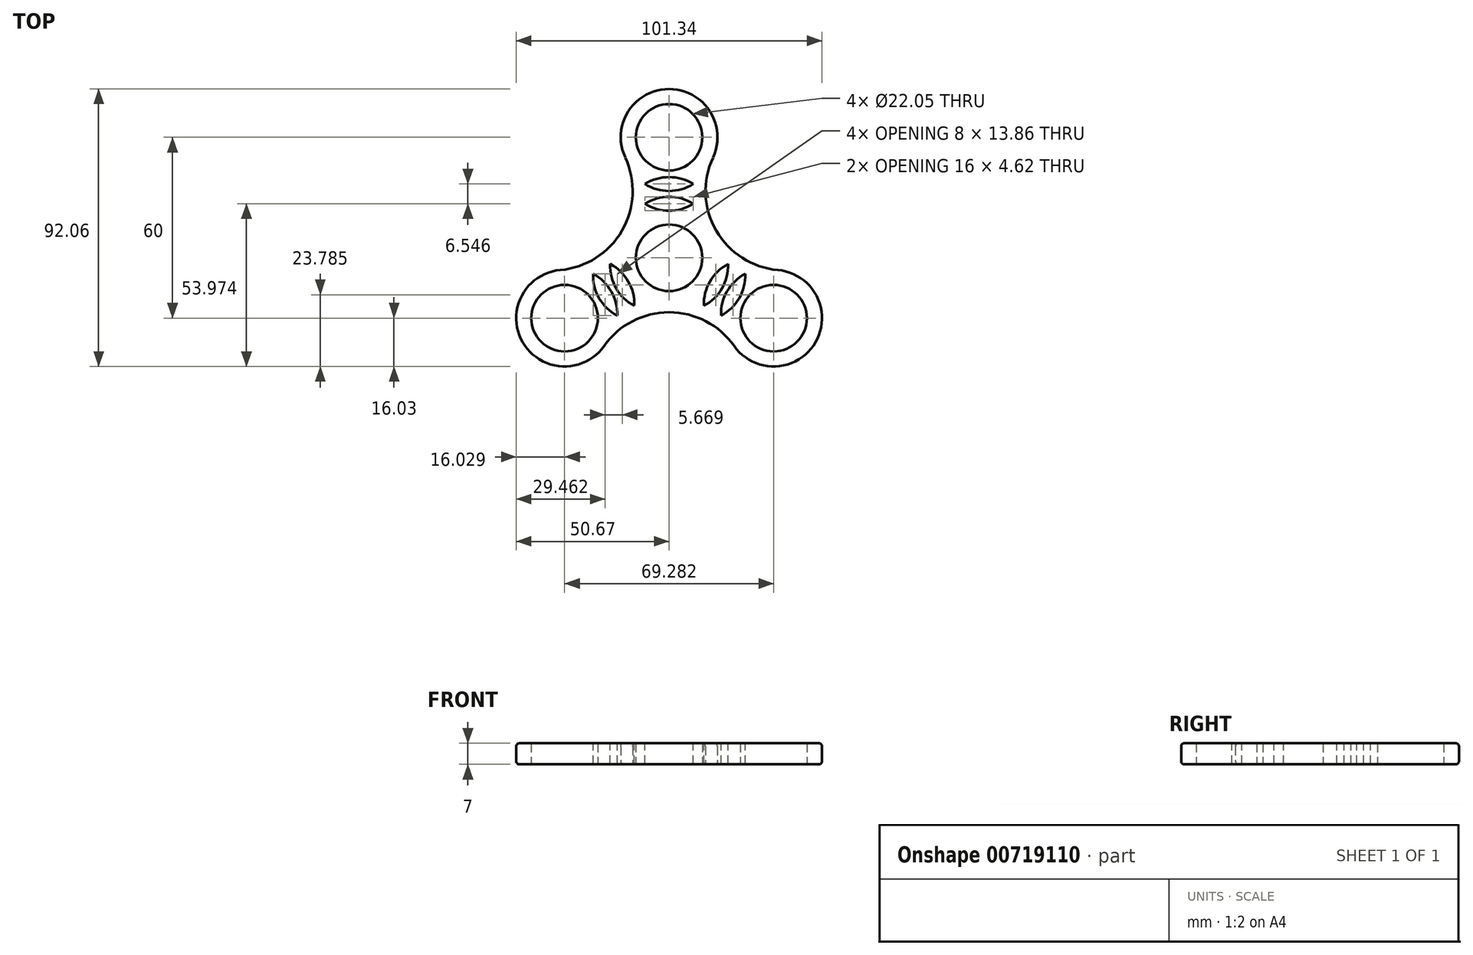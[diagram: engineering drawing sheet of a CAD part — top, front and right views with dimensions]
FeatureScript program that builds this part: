
annotation { "Feature Type Name" : "Feature", "Feature Type Description" : "" }
export const myFeature = defineFeature(function(context is Context, id is Id, definition is map)
    precondition{}
    {
        {
            var Q0;
            Q0=qCreatedBy(makeId("Top.planeOp"),FACE);
            var sketch = newSketch(context, id + "F0", { "sketchPlane" : qUnion([Q0])});
            skCircle(sketch, "E0", {"center": v(0, 0) * mm, "radius": 11.03 * mm});
            skCircle(sketch, "E1", {"center": v(0, 40) * mm, "radius": 11.03 * mm});
            skCircle(sketch, "E2.0", {"center": v(0, 40) * mm, "radius": 16.02 * mm});
            skCircle(sketch, "E3.0", {"center": v(0, 0) * mm, "radius": 18.02 * mm});
            skArc(sketch, "E4", {"start": v(-15.6, 9.01) * mm, "mid": v(-12.11, 21) * mm, "end": v(-14.53, 33.25) * mm});
            skLineSegment(sketch, "E5", {"start": v(0, -22.67) * mm, "end": v(0, 73.3) * mm, "construction": true});
            skArc(sketch, "E6.MirrorCS", {"start": v(15.6, 9.01) * mm, "mid": v(12.11, 21) * mm, "end": v(14.53, 33.25) * mm});
            skArc(sketch, "E7.1.0", {"start": v(0, -18.02) * mm, "mid": v(-12.13, -20.99) * mm, "end": v(-21.53, -29.21) * mm});
            skArc(sketch, "E7.1.1", {"start": v(-15.61, 9.01) * mm, "mid": v(-24.24, -0.01) * mm, "end": v(-36.06, -4.04) * mm});
            skCircle(sketch, "E7.1.2", {"center": v(-34.64, -20) * mm, "radius": 16.02 * mm});
            skCircle(sketch, "E7.1.3", {"center": v(-34.64, -20) * mm, "radius": 11.03 * mm});
            skArc(sketch, "E7.2.0", {"start": v(15.61, 9.01) * mm, "mid": v(24.24, -0.01) * mm, "end": v(36.06, -4.04) * mm});
            skArc(sketch, "E7.2.1", {"start": v(0, -18.02) * mm, "mid": v(12.13, -20.99) * mm, "end": v(21.53, -29.21) * mm});
            skCircle(sketch, "E7.2.2", {"center": v(34.64, -20) * mm, "radius": 16.02 * mm});
            skCircle(sketch, "E7.2.3", {"center": v(34.64, -20) * mm, "radius": 11.03 * mm});
            skSolve(sketch);
        }
        {
            var Q0;
            Q0=qSketchRegion(id+"F0",true);
            var Q1;
            Q1=makeQuery(id+"F0.imprint","IMPRINT",FACE,{"disambiguationData":[TD([[makeQuery(id+"F0.imprint","IMPRINT",EDGE,{"derivedFrom":sQuery(id+"F0.wireOp",EDGE,"E0")}),-1.0]])]});
            extrude(context, id + "F1", {"entities" : qUnion([Q0, Q1]), "depth" : 7 * mm, "offsetDistance" : 25 * mm});
        }
        {
            var Q0;
            Q0=makeQuery(id+"F1.opExtrude","SWEPT_FACE",FACE,{"disambiguationData":[OSD([sQuery(id+"F0.wireOp",EDGE,"E2.0")])]});
            var Q1;
            Q1=makeQuery(id+"F1.opExtrude","SWEPT_FACE",FACE,{"disambiguationData":[OSD([sQuery(id+"F0.wireOp",EDGE,"E4")])]});
            var Q2;
            Q2=makeQuery(id+"F1.opExtrude","SWEPT_FACE",FACE,{"disambiguationData":[OSD([sQuery(id+"F0.wireOp",EDGE,"E7.1.1")])]});
            var Q3;
            Q3=makeQuery(id+"F1.opExtrude","SWEPT_FACE",FACE,{"disambiguationData":[OSD([sQuery(id+"F0.wireOp",EDGE,"E7.1.2")])]});
            var Q4;
            Q4=makeQuery(id+"F1.opExtrude","SWEPT_FACE",FACE,{"disambiguationData":[OSD([sQuery(id+"F0.wireOp",EDGE,"E7.2.1")])]});
            fillet(context, id + "F2", {"entities" : qUnion([Q0, Q1, Q2, Q3, Q4]), "radius" : 1 * mm, "tangentPropagation" : true, "allowEdgeOverflow" : false});
        }
        {
            var Q0;
            Q0=makeQuery(id+"F1.opExtrude","CAP_FACE",FACE,{"disambiguationData":[OSD([sQuery(id+"F0.wireOp",EDGE,"E0"),sQuery(id+"F0.wireOp",EDGE,"E1"),sQuery(id+"F0.wireOp",EDGE,"E2.0"),sQuery(id+"F0.wireOp",EDGE,"E3.0"),sQuery(id+"F0.wireOp",EDGE,"E4"),sQuery(id+"F0.wireOp",EDGE,"E6.MirrorCS"),sQuery(id+"F0.wireOp",EDGE,"E7.1.0"),sQuery(id+"F0.wireOp",EDGE,"E7.1.1"),sQuery(id+"F0.wireOp",EDGE,"E7.1.2"),sQuery(id+"F0.wireOp",EDGE,"E7.1.3"),sQuery(id+"F0.wireOp",EDGE,"E7.2.0"),sQuery(id+"F0.wireOp",EDGE,"E7.2.1"),sQuery(id+"F0.wireOp",EDGE,"E7.2.2"),sQuery(id+"F0.wireOp",EDGE,"E7.2.3")])],"isStart":false});
            var sketch = newSketch(context, id + "F3", { "sketchPlane" : qUnion([Q0])});
            skArc(sketch, "E8", {"start": v(8, 24.49) * mm, "mid": v(0, 26.8) * mm, "end": v(-8, 24.49) * mm});
            skArc(sketch, "E9", {"start": v(-8, 24.49) * mm, "mid": v(0, 22.18) * mm, "end": v(8, 24.49) * mm});
            skLineSegment(sketch, "E10", {"start": v(0, 37.2) * mm, "end": v(0, 11.78) * mm, "construction": true});
            skPoint(sketch, "E11", {"position": v(0, 26.8) * mm});
            skLineSegment(sketch, "E12", {"start": v(-8, 24.49) * mm, "end": v(-8, 37.2) * mm, "construction": true});
            skLineSegment(sketch, "E13", {"start": v(-8, 24.49) * mm, "end": v(-8, 11.78) * mm, "construction": true});
            skArc(sketch, "E14", {"start": v(8, 17.94) * mm, "mid": v(0, 20.25) * mm, "end": v(-8, 17.94) * mm});
            skArc(sketch, "E15", {"start": v(-8, 17.94) * mm, "mid": v(0, 15.63) * mm, "end": v(8, 17.94) * mm});
            skLineSegment(sketch, "E16", {"start": v(0, 30.64) * mm, "end": v(0, 5.24) * mm, "construction": true});
            skLineSegment(sketch, "E17", {"start": v(-8, 17.94) * mm, "end": v(-8, 30.64) * mm, "construction": true});
            skLineSegment(sketch, "E18", {"start": v(-8, 17.94) * mm, "end": v(-8, 5.24) * mm, "construction": true});
            skArc(sketch, "E19.1.0", {"start": v(-11.54, -15.9) * mm, "mid": v(-13.54, -7.82) * mm, "end": v(-19.54, -2.04) * mm});
            skArc(sketch, "E19.1.1", {"start": v(-19.54, -2.04) * mm, "mid": v(-17.54, -10.13) * mm, "end": v(-11.54, -15.9) * mm});
            skArc(sketch, "E19.1.2", {"start": v(-17.2, -19.17) * mm, "mid": v(-19.2, -11.1) * mm, "end": v(-25.2, -5.32) * mm});
            skArc(sketch, "E19.1.3", {"start": v(-25.2, -5.32) * mm, "mid": v(-23.2, -13.4) * mm, "end": v(-17.2, -19.17) * mm});
            skArc(sketch, "E19.2.0", {"start": v(19.54, -2.04) * mm, "mid": v(13.54, -7.82) * mm, "end": v(11.54, -15.9) * mm});
            skArc(sketch, "E19.2.1", {"start": v(11.54, -15.9) * mm, "mid": v(17.54, -10.13) * mm, "end": v(19.54, -2.04) * mm});
            skArc(sketch, "E19.2.2", {"start": v(25.2, -5.32) * mm, "mid": v(19.2, -11.1) * mm, "end": v(17.2, -19.17) * mm});
            skArc(sketch, "E19.2.3", {"start": v(17.2, -19.17) * mm, "mid": v(23.2, -13.4) * mm, "end": v(25.2, -5.32) * mm});
            skPoint(sketch, "E19.center", {"position": v(0, 0) * mm});
            skSolve(sketch);
        }
        {
            var Q0;
            Q0 = qSketchRegion(id + "F3", true);
            extrude(context, id + "F4", {"entities" : qUnion([Q0]), "operationType" : NewBodyOperationType.REMOVE, "oppositeDirection" : true, "depth" : 25 * mm, "offsetDistance" : 25 * mm});
        }
    });
